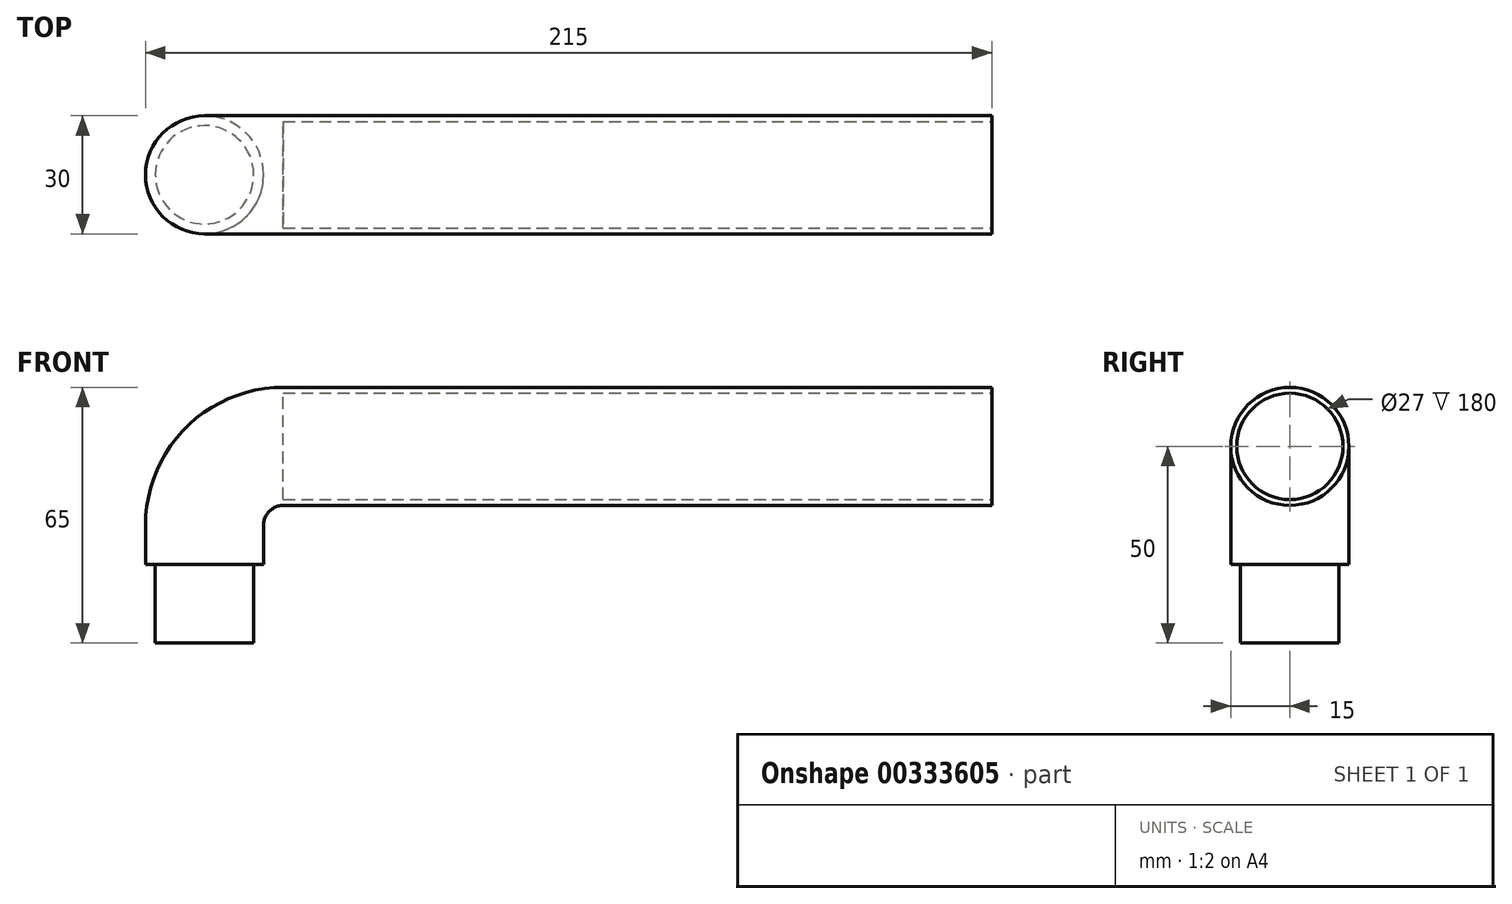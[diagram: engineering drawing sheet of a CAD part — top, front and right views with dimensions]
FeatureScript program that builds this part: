
annotation { "Feature Type Name" : "Feature", "Feature Type Description" : "" }
export const myFeature = defineFeature(function(context is Context, id is Id, definition is map)
    precondition{}
    {
        {
            var Q0;
            Q0=qCreatedBy(makeId("Front.planeOp"),FACE);
            var sketch = newSketch(context, id + "F0", { "sketchPlane" : qUnion([Q0])});
            skLineSegment(sketch, "E0", {"start": v(0, 0) * mm, "end": v(0, 30) * mm});
            skLineSegment(sketch, "E1", {"start": v(20, 50) * mm, "end": v(200, 50) * mm});
            skPoint(sketch, "E2.visualSharp", {"position": v(0, 50) * mm});
            skArc(sketch, "E2.filletArc", {"start": v(20, 50) * mm, "mid": v(5.86, 44.14) * mm, "end": v(0, 30) * mm});
            skSolve(sketch);
        }
        {
            var Q0;
            Q0=qCreatedBy(makeId("Top.planeOp"),FACE);
            var sketch = newSketch(context, id + "F1", { "sketchPlane" : qUnion([Q0])});
            skCircle(sketch, "E3", {"center": v(0, 0) * mm, "radius": 15 * mm});
            skSolve(sketch);
        }
        {
            var Q0;
            Q0=makeQuery(id+"F1.imprint","IMPRINT",FACE,{"disambiguationData":[TD([[makeQuery(id+"F1.imprint","IMPRINT",EDGE,{"derivedFrom":sQuery(id+"F1.wireOp",EDGE,"E3")}),1.0]])]});
            var Q1;
            Q1=sQuery(id+"F0.wireOp",EDGE,"E0");
            var Q2;
            Q2=sQuery(id+"F0.wireOp",EDGE,"E2.filletArc");
            var Q3;
            Q3=sQuery(id+"F0.wireOp",EDGE,"E1");
            sweep(context, id + "F2", {"profiles" : qUnion([Q0]), "path" : qUnion([Q1, Q2, Q3])});
        }
        {
            var Q0;
            Q0=qCreatedBy(makeId("Top.planeOp"),FACE);
            var sketch = newSketch(context, id + "F3", { "sketchPlane" : qUnion([Q0])});
            skCircle(sketch, "E4", {"center": v(0, 0) * mm, "radius": 12.5 * mm});
            skCircle(sketch, "E5", {"center": v(0, 0) * mm, "radius": 15 * mm});
            skSolve(sketch);
        }
        {
            var Q0;
            Q0=makeQuery(id+"F3.imprint","IMPRINT",FACE,{"disambiguationData":[TD([[makeQuery(id+"F3.imprint","IMPRINT",EDGE,{"derivedFrom":sQuery(id+"F3.wireOp",EDGE,"E4")}),-1.0]])]});
            extrude(context, id + "F4", {"entities" : qUnion([Q0]), "operationType" : NewBodyOperationType.REMOVE, "depth" : 20 * mm});
        }
        {
            var Q0;
            Q0=makeQuery(id+"F2.opSweep","CAP_FACE",FACE,{"disambiguationData":[OSD([sQuery(id+"F0.wireOp",VERTEX,"E1.end"),sQuery(id+"F1.wireOp",EDGE,"E3")])],"isStart":false});
            var sketch = newSketch(context, id + "F5", { "sketchPlane" : qUnion([Q0])});
            skCircle(sketch, "E6", {"center": v(0, 50) * mm, "radius": 13.5 * mm});
            skSolve(sketch);
        }
        {
            var Q0;
            Q0=makeQuery(id+"F5.imprint","IMPRINT",FACE,{"disambiguationData":[TD([[makeQuery(id+"F5.imprint","IMPRINT",EDGE,{"derivedFrom":sQuery(id+"F5.wireOp",EDGE,"E6")}),1.0]])]});
            extrude(context, id + "F6", {"entities" : qUnion([Q0]), "operationType" : NewBodyOperationType.REMOVE, "oppositeDirection" : true, "depth" : 180 * mm});
        }
    });
